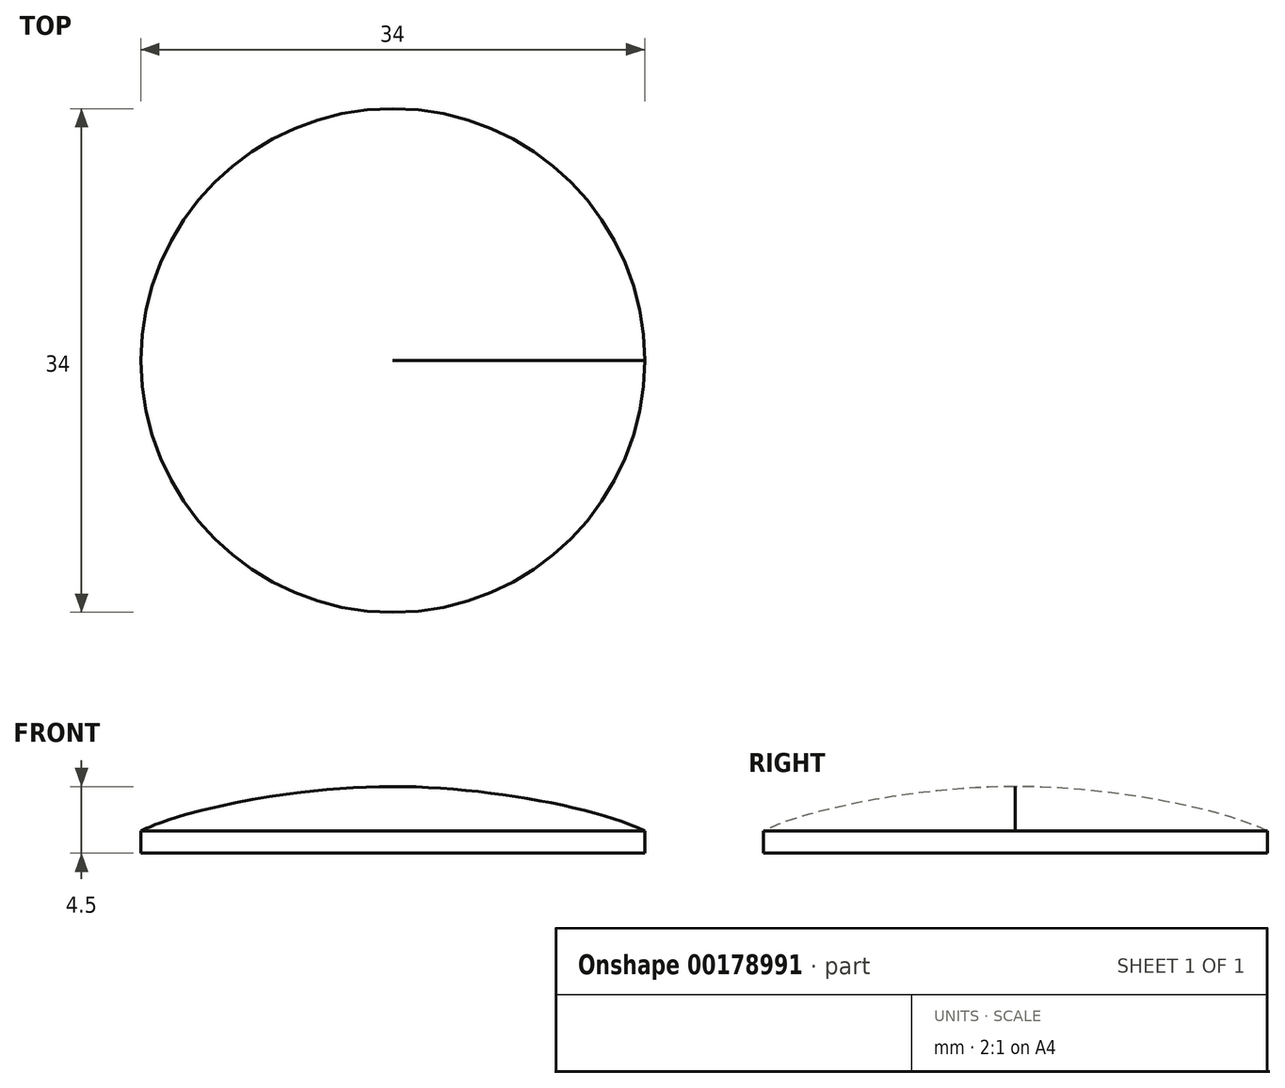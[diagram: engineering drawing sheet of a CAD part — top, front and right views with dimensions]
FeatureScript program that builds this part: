
annotation { "Feature Type Name" : "Feature", "Feature Type Description" : "" }
export const myFeature = defineFeature(function(context is Context, id is Id, definition is map)
    precondition{}
    {
        {
            var Q0;
            Q0=qCreatedBy(makeId("Front.planeOp"),FACE);
            var sketch = newSketch(context, id + "F0", { "sketchPlane" : qUnion([Q0])});
            skLineSegment(sketch, "E0.bottom", {"start": v(17, -2.25) * mm, "end": v(-17, -2.25) * mm, "construction": true});
            skLineSegment(sketch, "E0.top", {"start": v(17, 2.25) * mm, "end": v(-17, 2.25) * mm, "construction": true});
            skLineSegment(sketch, "E0.left", {"start": v(17, -2.25) * mm, "end": v(17, 2.25) * mm, "construction": true});
            skLineSegment(sketch, "E0.right", {"start": v(-17, -2.25) * mm, "end": v(-17, 2.25) * mm, "construction": true});
            skPoint(sketch, "E0.middle", {"position": v(0, 0) * mm});
            skLineSegment(sketch, "E1", {"start": v(17, -2.25) * mm, "end": v(17, -0.75) * mm});
            skFitSpline(sketch, "E2", {"points": [v(0, 2.25) * mm, v(17, -0.75) * mm], "startDerivative": vector(17.9, 0) * mm, "endDerivative": vector(10.02, -4.91) * mm});
            skLineSegment(sketch, "E3", {"start": v(17, -2.25) * mm, "end": v(0, -2.25) * mm});
            skLineSegment(sketch, "E4", {"start": v(0, -6.4) * mm, "end": v(0, -2.25) * mm, "construction": true});
            skLineSegment(sketch, "E5", {"start": v(0, -2.25) * mm, "end": v(0, 2.25) * mm});
            skSolve(sketch);
        }
        {
            var Q0;
            Q0 = qSketchRegion(id + "F0", true);
            var Q1;
            Q1=sQuery(id+"F0.wireOp",EDGE,"E4");
            revolve(context, id + "F1", {"entities" : qUnion([Q0]), "axis" : qUnion([Q1]), "revolveType" : RevolveType.FULL});
        }
    });
